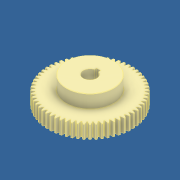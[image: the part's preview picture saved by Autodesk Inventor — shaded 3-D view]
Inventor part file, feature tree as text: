
AUTODESK INVENTOR PART (.ipt)
format: ipt  version: 2018 (Build 220112000, 112)  size: 969,728 bytes
history: native  units: mm
features: extrude x2, sketch x1, pattern_circular x1
ambient origin geometry x8: Origin, YZ Plane, XZ Plane, XY Plane, X Axis, Y Axis, Z Axis, Center Point
bodies: Solid1 (feature_tree)
feature tree (4):
  extrude  "Extrusion3"  Depth=1.4mm
  extrude  "Extrusion2"  Depth=5.0mm
  sketch  "Sketch3"  dims[d2=3.0mm d3=1.4mm d4=5.0mm d5=1.5mm d6=0.0mm d7=0.0mm d8=3.0mm d9=1.4mm d10=5.0mm d11=0.0mm d12=0.0mm]
  pattern_circular  "CirPattern1"
